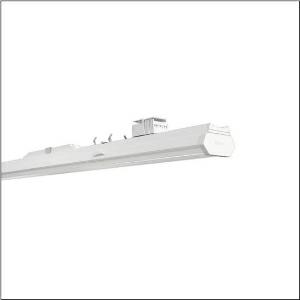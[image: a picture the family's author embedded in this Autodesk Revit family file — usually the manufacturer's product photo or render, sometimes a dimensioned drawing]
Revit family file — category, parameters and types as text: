
# Revit family: licross_r__11_protected_mo_51tp11dn59xg_8616
name_source: partatom
category: Lighting Fixtures
units: mm (PartAtom-declared; Revit-internal decimal feet)

## family parameters
Cut with Voids When Loaded = No
Host = Face
Light Source = No
Part Type = Normal
Room Calculation Point = No
Round Connector Dimension = Use Diameter
Shared = No

## types (1)
- --- (1 x LED, 9100 lm, 52.7 W, 5000K)
    Apparent Load = 53 VA
    CIE Flux Codes = 83 94 98 100 100
    Color Rendering = 80
    Color Temperature = 5000K
    Default Elevation = 1800 mm
    Description = Licross® 11 Protected MO, luminaire insert, of sheet steel, galvanised, coil coated, white, length: 1.500mm, width: 90mm, height: 101mm, LED rated luminous flux: 9.100lm, light colour: 850, control gear: DALI 2, with plug, 5-pole, with phase selection, mains connection: 220..240V, AC, 50/60Hz, rated input power: 53W, internal wiring halogen-free, primary light control with lens, of plastic, primary optical cover: cover, of PMMA, light emission: direct distribution, primary light characteristic: symmetric, protection rating (complete): IP64, insulation class (complete): insulation class I (protective earthing), certification: CE, ENEC, VDE, UKCA, protection symbol: D if used in an environment with conductive dust loads with corresponding accessories, impact resistance: IK06, permissible ambient temperature for indoor applications: -25..+35°C, LABS conformity tested according to VDMA 24364:2018-05, reducing of maximum allowable ambient temperature of 5°C with ceiling mounting, corresponds to IFS (International Featured Standards) requirements for safety and quality in the food industry, packaging unit: 1 piece
    Height = 92 mm
    Lamp = 1 x LED
    Lamp Light Flux = 9100 lm
    Lamp Power = 52.7 W
    Lamp count = 1
    Length = 1500 mm
    Luminous efficacy = 173 lm/W
    Manufacturer = Siteco
    ModVariant = No
    Model = 51TP11DN59XG
    Mounting Place = Ceiling
    Mounting Type = Pendant
    Number of Poles = 1
    OnlyDefault = Yes
    Power Factor = 1
    Product Name = Licross® 11 Protected MO
    Product group = luminaire insert | ceiling pendant
    ProductGroupID = 902
    Protection Class = Protection class I
    Protection Degree = IP 64
    RLX_Detail_Level = 1
    RLX_Emergency_Light_Flux = 0 lm
    RLX_Emergency_Type = 0
    RLX_Emergency_Type_DB = No
    RlxData = <blob elided: 24117 chars, md5=98a938d1>
    Socket = socket
    Standby Power = 0 W
    System Light Flux = 9100 lm
    System Power = 53 W
    Type Comments = factory setting: luminous flux: 100 % | dim-lin: 254 | 350 mA
    Type Image = l_1256148.jpg
    URL = http://relux.com
    VarID = @adj_018403
    Voltage = 0 V
    Weight = 0.00 kg
    Width = 88 mm

## geometry (parser evidence)
native form markers: Blend x4, Sweep x11
no freeform markers — native parametric forms only
